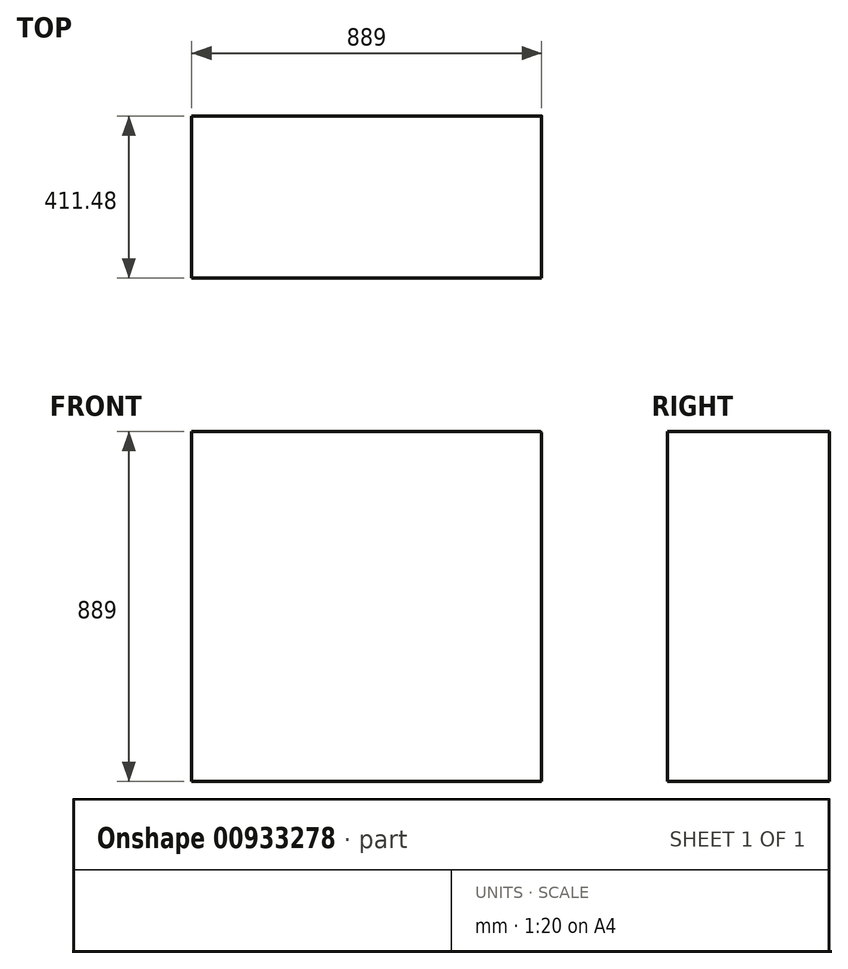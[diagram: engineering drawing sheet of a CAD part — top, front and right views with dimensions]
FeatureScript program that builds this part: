
annotation { "Feature Type Name" : "Feature", "Feature Type Description" : "" }
export const myFeature = defineFeature(function(context is Context, id is Id, definition is map)
    precondition{}
    {
        {
            var Q0;
            Q0=qCreatedBy(makeId("Front.planeOp"),FACE);
            var sketch = newSketch(context, id + "F0", { "sketchPlane" : qUnion([Q0])});
            skLineSegment(sketch, "E0.bottom", {"start": v(444.5, -444.5) * mm, "end": v(-444.5, -444.5) * mm});
            skLineSegment(sketch, "E0.top", {"start": v(444.5, 444.5) * mm, "end": v(-444.5, 444.5) * mm});
            skLineSegment(sketch, "E0.left", {"start": v(444.5, -444.5) * mm, "end": v(444.5, 444.5) * mm});
            skLineSegment(sketch, "E0.right", {"start": v(-444.5, -444.5) * mm, "end": v(-444.5, 444.5) * mm});
            skPoint(sketch, "E0.middle", {"position": v(0, 0) * mm});
            skSolve(sketch);
        }
        {
            var Q0;
            Q0 = qSketchRegion(id + "F0", true);
            extrude(context, id + "F1", {"entities" : qUnion([Q0]), "depth" : 411.48 * mm, "offsetDistance" : 25.4 * mm});
        }
        {
            var Q0;
            Q0=makeQuery(id+"F1.opExtrude","SWEPT_EDGE",EDGE,{"disambiguationData":[OSD([sQuery(id+"F0.wireOp",EDGE,"E0.top"),sQuery(id+"F0.wireOp",EDGE,"E0.left")])]});
            fillet(context, id + "F2", {"entities" : qUnion([Q0]), "radius" : 5.08 * mm, "tangentPropagation" : true, "allowEdgeOverflow" : false});
        }
    });
